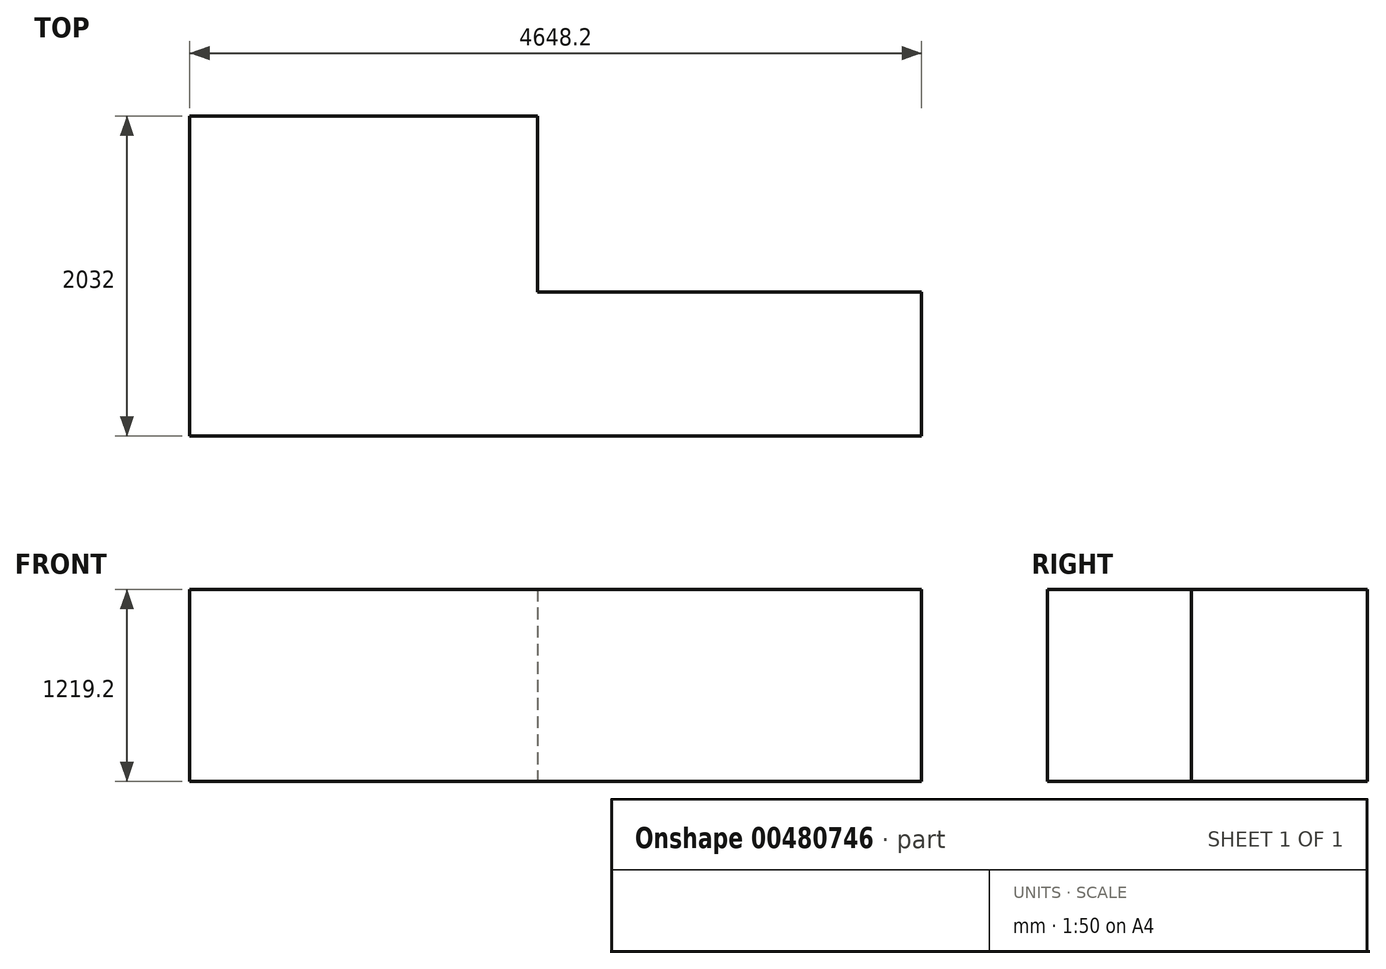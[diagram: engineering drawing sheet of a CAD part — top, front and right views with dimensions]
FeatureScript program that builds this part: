
annotation { "Feature Type Name" : "Feature", "Feature Type Description" : "" }
export const myFeature = defineFeature(function(context is Context, id is Id, definition is map)
    precondition{}
    {
        {
            var Q0;
            Q0=qCreatedBy(makeId("Top.planeOp"),FACE);
            var sketch = newSketch(context, id + "F0", { "sketchPlane" : qUnion([Q0])});
            skLineSegment(sketch, "E0.bottom", {"start": v(2209.8, 2032) * mm, "end": v(0, 2032) * mm});
            skLineSegment(sketch, "E0.top", {"start": v(2209.8, 0) * mm, "end": v(0, 0) * mm});
            skLineSegment(sketch, "E0.left", {"start": v(2209.8, 2032) * mm, "end": v(2209.8, 914.4) * mm});
            skLineSegment(sketch, "E0.right", {"start": v(0, 2032) * mm, "end": v(0, 0) * mm});
            skPoint(sketch, "E0.middle", {"position": v(1104.9, 1016) * mm});
            skLineSegment(sketch, "E1", {"start": v(2209.8, 0) * mm, "end": v(4648.2, 0) * mm});
            skLineSegment(sketch, "E2", {"start": v(4648.2, 0) * mm, "end": v(4648.2, 914.4) * mm});
            skLineSegment(sketch, "E3", {"start": v(4648.2, 914.4) * mm, "end": v(2209.8, 914.4) * mm});
            skSolve(sketch);
        }
        {
            var Q0;
            Q0=makeQuery(id+"F0.imprint","IMPRINT",FACE,{"disambiguationData":[TD([[makeQuery(id+"F0.imprint","IMPRINT",EDGE,{"derivedFrom":sQuery(id+"F0.wireOp",EDGE,"E0.bottom")}),1.0]])]});
            extrude(context, id + "F1", {"entities" : qUnion([Q0]), "depth" : 1219.2 * mm});
        }
    });
